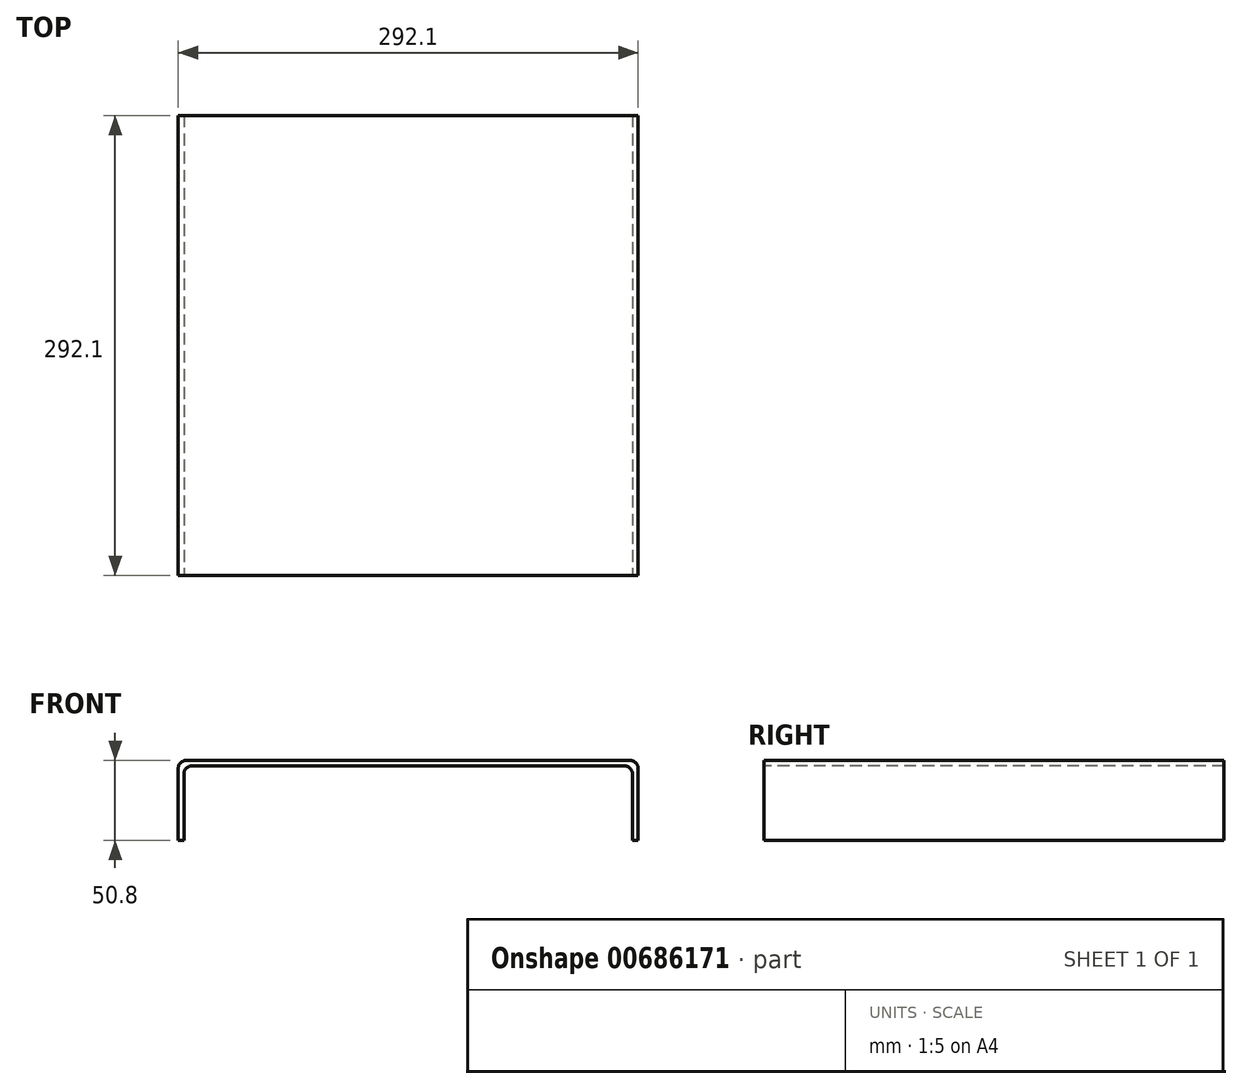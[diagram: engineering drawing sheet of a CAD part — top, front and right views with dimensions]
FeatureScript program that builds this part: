
annotation { "Feature Type Name" : "Feature", "Feature Type Description" : "" }
export const myFeature = defineFeature(function(context is Context, id is Id, definition is map)
    precondition{}
    {
        {
            var Q0;
            Q0=qCreatedBy(makeId("Top.planeOp"),FACE);
            var sketch = newSketch(context, id + "F0", { "sketchPlane" : qUnion([Q0])});
            skLineSegment(sketch, "E0.bottom", {"start": v(-203, 143.88) * mm, "end": v(89.1, 143.88) * mm});
            skLineSegment(sketch, "E0.top", {"start": v(-203, -148.22) * mm, "end": v(89.1, -148.22) * mm});
            skLineSegment(sketch, "E0.left", {"start": v(-203, 143.88) * mm, "end": v(-203, -148.22) * mm});
            skLineSegment(sketch, "E0.right", {"start": v(89.1, 143.88) * mm, "end": v(89.1, -148.22) * mm});
            skSolve(sketch);
        }
        {
            var Q0;
            Q0 = qSketchRegion(id + "F0", true);
            extrude(context, id + "F1", {"entities" : qUnion([Q0]), "depth" : 50.8 * mm, "offsetDistance" : 25.4 * mm});
        }
        {
            var Q0;
            Q0=makeQuery(id+"F1.opExtrude","SWEPT_FACE",FACE,{"disambiguationData":[OSD([sQuery(id+"F0.wireOp",EDGE,"E0.top")])]});
            var Q1;
            Q1=makeQuery(id+"F1.opExtrude","SWEPT_FACE",FACE,{"disambiguationData":[OSD([sQuery(id+"F0.wireOp",EDGE,"E0.bottom")])]});
            var Q2;
            Q2=makeQuery(id+"F1.opExtrude","CAP_FACE",FACE,{"disambiguationData":[OSD([sQuery(id+"F0.wireOp",EDGE,"E0.bottom"),sQuery(id+"F0.wireOp",EDGE,"E0.top"),sQuery(id+"F0.wireOp",EDGE,"E0.left"),sQuery(id+"F0.wireOp",EDGE,"E0.right")])],"isStart":true});
            shell(context, id + "F2", {"entities" : qUnion([Q0, Q1, Q2]), "thickness" : 3.57 * mm});
        }
        {
            var Q0;
            {var subQ0=sQuery(id+"F0.wireOp",EDGE,"E0.left");Q0=makeQuery(id+"F2.opShell","OFFSET_EDGE",EDGE,{"disambiguationData":[OSD([subQ0]),TDD([makeQuery(id+"F1.opExtrude","CAP_EDGE",EDGE,{"disambiguationData":[OSD([subQ0])],"isStart":false})])]});}
            var Q1;
            {var subQ0=sQuery(id+"F0.wireOp",EDGE,"E0.right");Q1=makeQuery(id+"F2.opShell","OFFSET_EDGE",EDGE,{"disambiguationData":[OSD([subQ0]),TDD([makeQuery(id+"F1.opExtrude","CAP_EDGE",EDGE,{"disambiguationData":[OSD([subQ0])],"isStart":false})])]});}
            var Q2;
            Q2=makeQuery(id+"F1.opExtrude","CAP_EDGE",EDGE,{"disambiguationData":[OSD([sQuery(id+"F0.wireOp",EDGE,"E0.left")])],"isStart":false});
            var Q3;
            Q3=makeQuery(id+"F1.opExtrude","CAP_EDGE",EDGE,{"disambiguationData":[OSD([sQuery(id+"F0.wireOp",EDGE,"E0.right")])],"isStart":false});
            fillet(context, id + "F3", {"entities" : qUnion([Q0, Q1, Q2, Q3]), "radius" : 5.08 * mm, "tangentPropagation" : true, "allowEdgeOverflow" : false});
        }
    });
